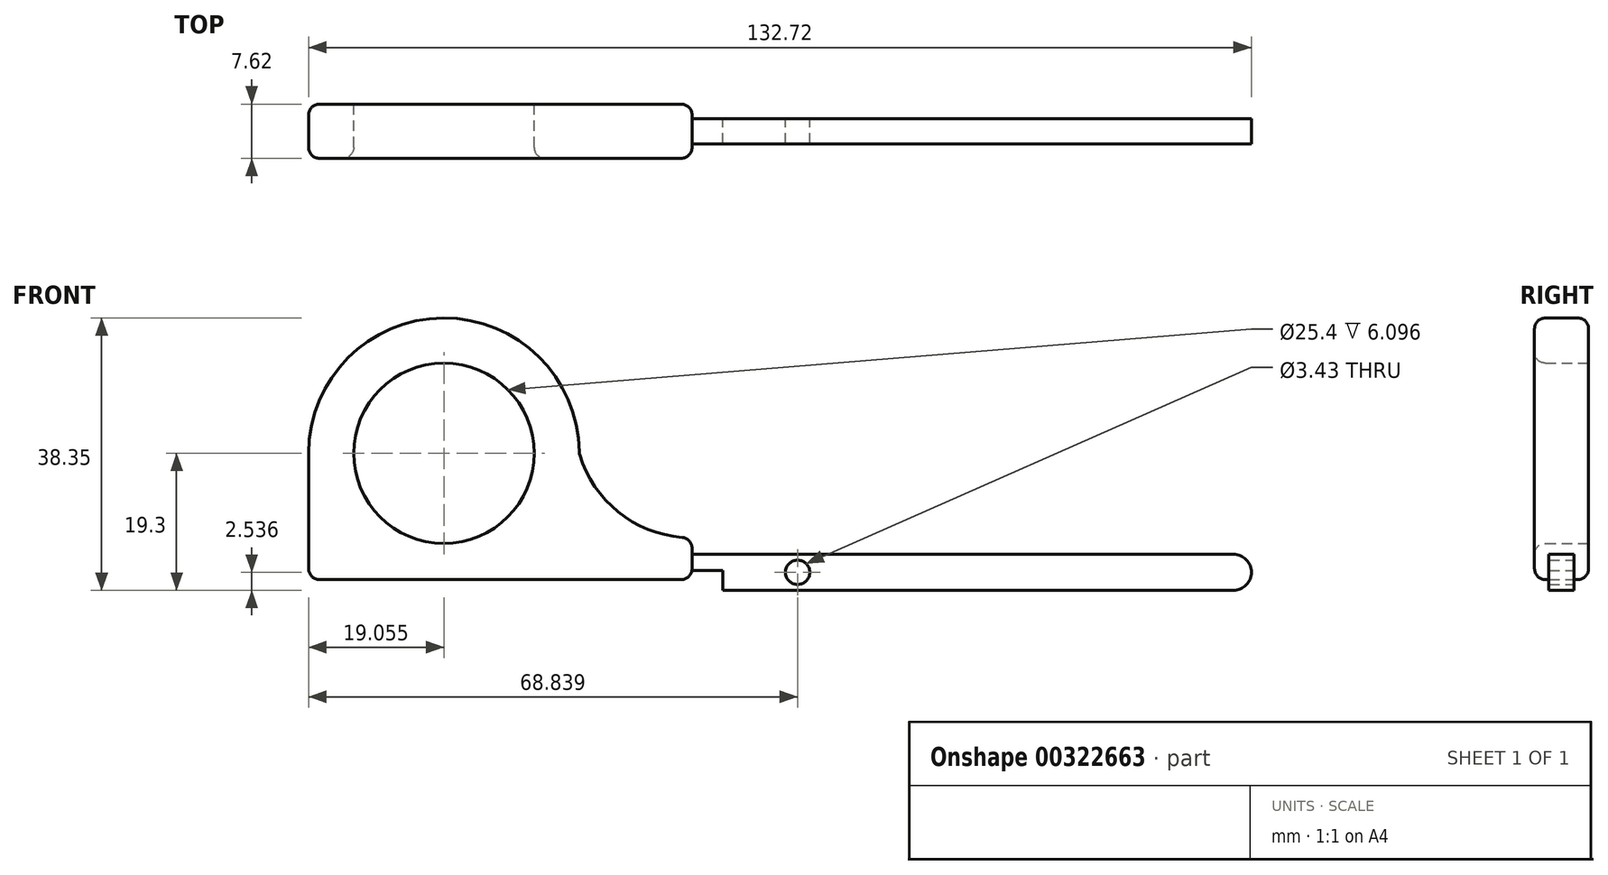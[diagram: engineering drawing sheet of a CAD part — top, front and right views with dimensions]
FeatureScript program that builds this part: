
annotation { "Feature Type Name" : "Feature", "Feature Type Description" : "" }
export const myFeature = defineFeature(function(context is Context, id is Id, definition is map)
    precondition{}
    {
        {
            var Q0;
            Q0=qCreatedBy(makeId("Front.planeOp"),FACE);
            var sketch = newSketch(context, id + "F0", { "sketchPlane" : qUnion([Q0])});
            skCircle(sketch, "E0", {"center": v(-45.13, 0) * mm, "radius": 12.7 * mm});
            skLineSegment(sketch, "E1", {"start": v(-64.18, -12.94) * mm, "end": v(-64.18, 0) * mm});
            skPoint(sketch, "E2", {"position": v(-64.18, 0) * mm});
            skArc(sketch, "E3", {"start": v(-64.18, 0) * mm, "mid": v(-45.23, 19.05) * mm, "end": v(-26.08, 0.2) * mm});
            skLineSegment(sketch, "E4", {"start": v(-64.18, -12.94) * mm, "end": v(-64.18, -16.26) * mm});
            skLineSegment(sketch, "E5", {"start": v(-62.65, -17.78) * mm, "end": v(-11.72, -17.78) * mm});
            skLineSegment(sketch, "E6", {"start": v(-10.2, -16.26) * mm, "end": v(-10.2, -13.37) * mm});
            skPoint(sketch, "E7.visualSharp", {"position": v(-64.18, -17.78) * mm});
            skArc(sketch, "E7.filletArc", {"start": v(-64.18, -16.26) * mm, "mid": v(-63.73, -17.33) * mm, "end": v(-62.65, -17.78) * mm});
            skArc(sketch, "E8", {"start": v(-26.01, -0.22) * mm, "mid": v(-20.59, -8.25) * mm, "end": v(-11.6, -11.85) * mm});
            skPoint(sketch, "E9.visualSharp", {"position": v(-10.2, -11.91) * mm});
            skArc(sketch, "E9.filletArc", {"start": v(-10.2, -13.37) * mm, "mid": v(-10.6, -12.34) * mm, "end": v(-11.6, -11.85) * mm});
            skPoint(sketch, "E10.visualSharp", {"position": v(-10.2, -17.78) * mm});
            skArc(sketch, "E10.filletArc", {"start": v(-11.72, -17.78) * mm, "mid": v(-10.65, -17.33) * mm, "end": v(-10.2, -16.26) * mm});
            skPoint(sketch, "E11.visualSharp", {"position": v(-26.08, 0) * mm});
            skArc(sketch, "E11.filletArc", {"start": v(-26.08, 0.2) * mm, "mid": v(-26.06, 0) * mm, "end": v(-26.01, -0.22) * mm});
            skLineSegment(sketch, "E12", {"start": v(-10.2, -14.22) * mm, "end": v(66, -14.22) * mm});
            skLineSegment(sketch, "E13", {"start": v(-10.2, -16.51) * mm, "end": v(-5.88, -16.51) * mm});
            skLineSegment(sketch, "E14", {"start": v(-5.88, -16.51) * mm, "end": v(-5.88, -19.3) * mm});
            skLineSegment(sketch, "E15", {"start": v(-5.88, -19.3) * mm, "end": v(66, -19.3) * mm});
            skPoint(sketch, "E16", {"position": v(4.66, -19.3) * mm});
            skCircle(sketch, "E17", {"center": v(4.66, -16.76) * mm, "radius": 1.71 * mm});
            skPoint(sketch, "E18.orphan", {"position": v(4.66, -14.22) * mm});
            skLineSegment(sketch, "E19", {"start": v(-10.2, -16.51) * mm, "end": v(-10.22, -16.51) * mm});
            skArc(sketch, "E20", {"start": v(66, -19.3) * mm, "mid": v(68.54, -16.76) * mm, "end": v(66, -14.22) * mm});
            skLineSegment(sketch, "E21", {"start": v(4.66, -14.22) * mm, "end": v(4.66, -15.05) * mm, "construction": true});
            skLineSegment(sketch, "E22", {"start": v(4.66, -19.3) * mm, "end": v(4.66, -18.48) * mm, "construction": true});
            skSolve(sketch);
        }
        {
            var Q0;
            Q0=makeQuery(id+"F0.imprint","IMPRINT",FACE,{"disambiguationData":[TD([[makeQuery(id+"F0.imprint","IMPRINT",EDGE,{"derivedFrom":sQuery(id+"F0.wireOp",EDGE,"E0")}),-1.0]])]});
            extrude(context, id + "F1", {"entities" : qUnion([Q0]), "endBound" : BoundingType.SYMMETRIC, "depth" : 7.62 * mm});
        }
        {
            var Q0;
            {var subQ0=sQuery(id+"F0.wireOp",EDGE,"E12");Q0=makeQuery(id+"F0.imprint","IMPRINT",FACE,{"disambiguationData":[TD([[makeQuery(id+"F0.imprint","IMPRINT",EDGE,{"derivedFrom":subQ0}),-1.0]])]});}
            extrude(context, id + "F2", {"entities" : qUnion([Q0]), "operationType" : NewBodyOperationType.ADD, "endBound" : BoundingType.SYMMETRIC, "depth" : 3.56 * mm});
        }
        {
            var Q0;
            Q0=makeQuery(id+"F1.opExtrude","CAP_EDGE",EDGE,{"disambiguationData":[OSD([sQuery(id+"F0.wireOp",EDGE,"E3")])],"isStart":false});
            var Q1;
            Q1=makeQuery(id+"F1.opExtrude","CAP_EDGE",EDGE,{"disambiguationData":[OSD([sQuery(id+"F0.wireOp",EDGE,"E3")])],"isStart":true});
            var Q2;
            Q2=makeQuery(id+"F1.opExtrude","CAP_EDGE",EDGE,{"disambiguationData":[OSD([sQuery(id+"F0.wireOp",EDGE,"E0")])],"isStart":false});
            fillet(context, id + "F3", {"entities" : qUnion([Q0, Q1, Q2]), "radius" : 1.52 * mm, "tangentPropagation" : true, "allowEdgeOverflow" : false});
        }
    });
